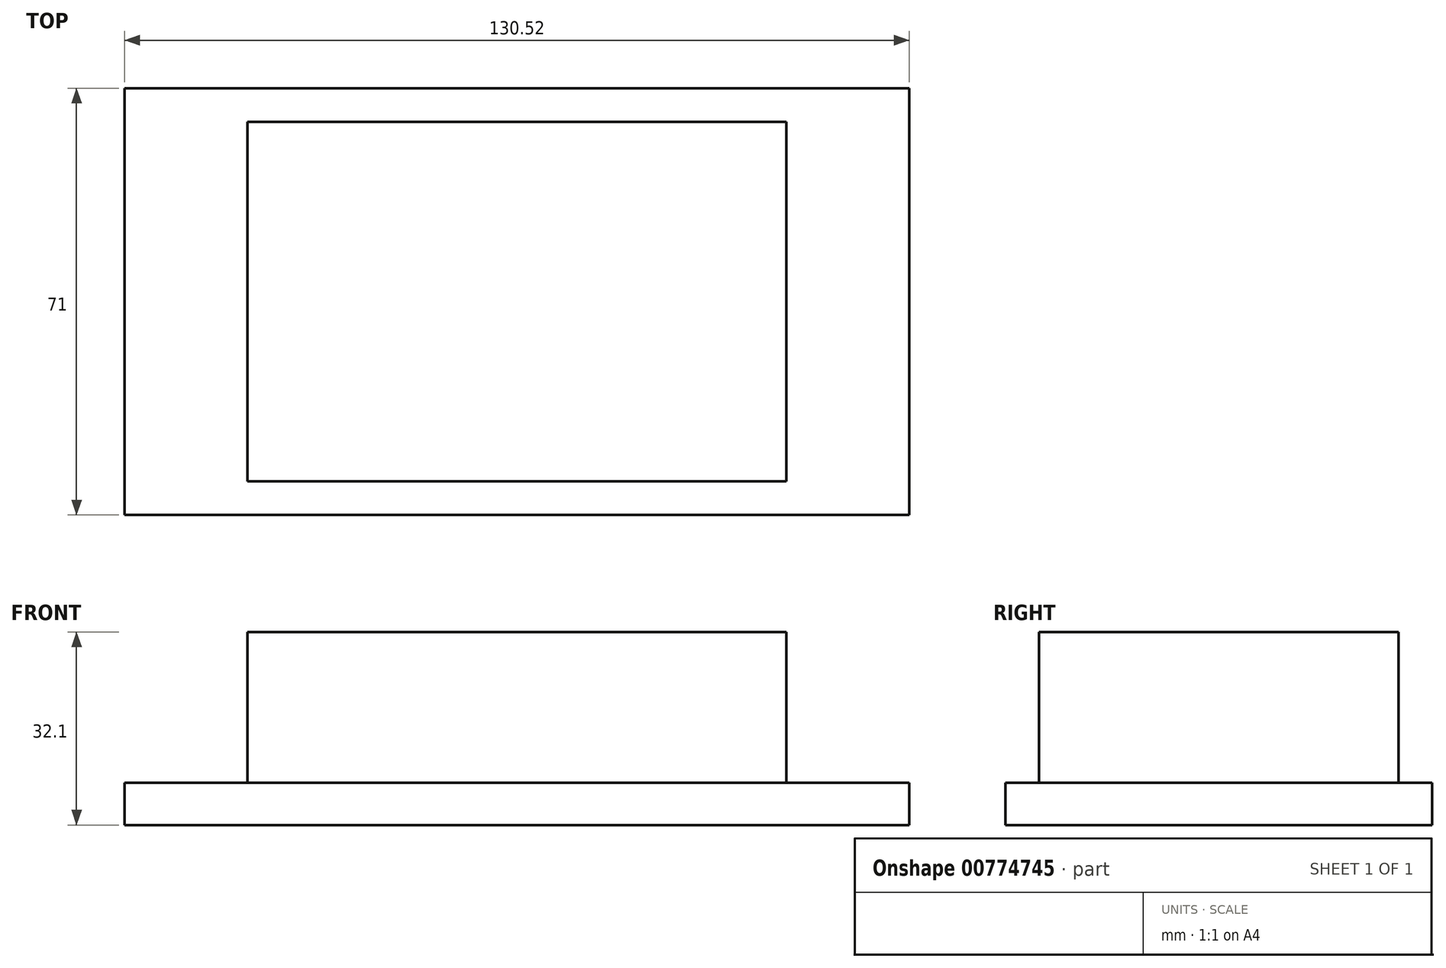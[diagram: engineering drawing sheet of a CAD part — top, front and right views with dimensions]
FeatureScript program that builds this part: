
annotation { "Feature Type Name" : "Feature", "Feature Type Description" : "" }
export const myFeature = defineFeature(function(context is Context, id is Id, definition is map)
    precondition{}
    {
        {
            var Q0;
            Q0=qCreatedBy(makeId("Top.planeOp"),FACE);
            var sketch = newSketch(context, id + "F0", { "sketchPlane" : qUnion([Q0])});
            skLineSegment(sketch, "E0.bottom", {"start": v(-65.26, 35.5) * mm, "end": v(65.26, 35.5) * mm});
            skLineSegment(sketch, "E0.top", {"start": v(-65.26, -35.5) * mm, "end": v(65.26, -35.5) * mm});
            skLineSegment(sketch, "E0.left", {"start": v(-65.26, 35.5) * mm, "end": v(-65.26, -35.5) * mm});
            skLineSegment(sketch, "E0.right", {"start": v(65.26, 35.5) * mm, "end": v(65.26, -35.5) * mm});
            skPoint(sketch, "E0.middle", {"position": v(0, 0) * mm});
            skSolve(sketch);
        }
        {
            var Q0;
            Q0 = qSketchRegion(id + "F0", true);
            extrude(context, id + "F1", {"entities" : qUnion([Q0]), "depth" : 7 * mm, "offsetDistance" : 25 * mm});
        }
        {
            var Q0;
            Q0=makeQuery(id+"F1.opExtrude","CAP_FACE",FACE,{"disambiguationData":[OSD([sQuery(id+"F0.wireOp",EDGE,"E0.bottom"),sQuery(id+"F0.wireOp",EDGE,"E0.top"),sQuery(id+"F0.wireOp",EDGE,"E0.left"),sQuery(id+"F0.wireOp",EDGE,"E0.right")])],"isStart":false});
            var sketch = newSketch(context, id + "F2", { "sketchPlane" : qUnion([Q0])});
            skLineSegment(sketch, "E1.bottom", {"start": v(-44.8, 29.92) * mm, "end": v(44.8, 29.92) * mm});
            skLineSegment(sketch, "E1.top", {"start": v(-44.8, -29.92) * mm, "end": v(44.8, -29.92) * mm});
            skLineSegment(sketch, "E1.left", {"start": v(-44.8, 29.92) * mm, "end": v(-44.8, -29.92) * mm});
            skLineSegment(sketch, "E1.right", {"start": v(44.8, 29.92) * mm, "end": v(44.8, -29.92) * mm});
            skPoint(sketch, "E1.middle", {"position": v(0, 0) * mm});
            skSolve(sketch);
        }
        {
            var Q0;
            Q0=makeQuery(id+"F2.imprint","IMPRINT",FACE,{"disambiguationData":[TD([[makeQuery(id+"F2.imprint","IMPRINT",EDGE,{"derivedFrom":sQuery(id+"F2.wireOp",EDGE,"E1.bottom")}),-1.0]])]});
            extrude(context, id + "F3", {"entities" : qUnion([Q0]), "operationType" : NewBodyOperationType.ADD, "depth" : .1 * mm, "offsetDistance" : 25 * mm});
        }
        {
            var Q0;
            Q0=makeQuery(id+"F3.opExtrude","CAP_FACE",FACE,{"disambiguationData":[OSD([sQuery(id+"F2.wireOp",EDGE,"E1.bottom"),sQuery(id+"F2.wireOp",EDGE,"E1.top"),sQuery(id+"F2.wireOp",EDGE,"E1.left"),sQuery(id+"F2.wireOp",EDGE,"E1.right")])],"isStart":false});
            extrude(context, id + "F4", {"entities" : qUnion([Q0]), "operationType" : NewBodyOperationType.ADD, "depth" : 25 * mm, "offsetDistance" : 25 * mm});
        }
    });
